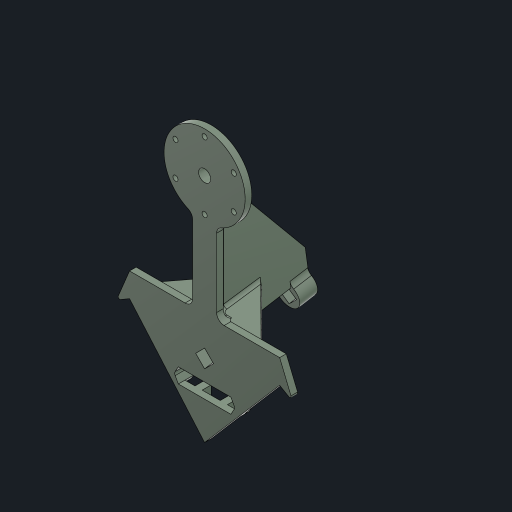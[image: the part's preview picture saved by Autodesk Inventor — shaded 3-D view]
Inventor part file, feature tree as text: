
AUTODESK INVENTOR PART (.ipt)
format: ipt  version: 2023 (Build 270158000, 158)  size: 518,144 bytes
history: native  units: mm
features: extrude x17, sketch x16, other x6, fillet x3, projected_geometry x2, mirror x1, hole x1, pattern_circular x1
ambient origin geometry x8: Origin, YZ Plane, XZ Plane, XY Plane, X Axis, Y Axis, Z Axis, Center Point
bodies: Body1 (feature_tree)
feature tree (47):
  other  "ソリッド1"
  sketch  "スケッチ1"
  extrude  "押し出し1"  Depth=2.2mm
  extrude  "押し出し2"  Depth=40.0mm
  extrude  "押し出し4"  Depth=14.3117mm
  extrude  "押し出し5"  Depth=8.0mm
  extrude  "爪"  Depth=180.0mm
  extrude  "押し出し17"  Depth=15.0mm
  extrude  "押し出し20"  Depth=14.0499mm
  extrude  "押し出し21"  Depth=30.0mm
  mirror  "ミラー1"
  extrude  "押し出し6"  Depth=25.0mm TaperAngle=0.0deg
  other  "作業平面2"
  extrude  "押し出し10"  Depth=4.0mm TaperAngle=0.0deg
  extrude  "ロッド穴"  Depth=1.6mm TaperAngle=0.0deg
  other  "作業平面3"
  extrude  "押し出し11"  TaperAngle=0.0deg  [1 undecoded]
  hole  "穴1"  [1 undecoded]
  pattern_circular  "円形状パターン1"  [2 undecoded]
  extrude  "穴延長"  Depth=1.4mm TaperAngle=0.0deg
  extrude  "押し出し12"  Depth=1.0mm
  extrude  "押し出し13"  Depth=4.2mm
  fillet  "フィレット2"  [1 undecoded]
  other  "YZ平面"
  other  "XZ平面"
  extrude  "押し出し22"  Depth=8.0mm
  fillet  "フィレット3"  Radius=5.0mm
  fillet  "フィレット4"  Radius=6.0mm
  extrude  "押し出し23"  Depth=22.4mm
  sketch  "スケッチ2"
  sketch  "スケッチ3"
  other  "作業平面1"
  sketch  "スケッチ6"
  sketch  "スケッチ7"
  sketch  "スケッチ8"
  projected_geometry  "投影ループ1"
  sketch  "スケッチ9"
  sketch  "スケッチ10"
  sketch  "スケッチ11"
  sketch  "スケッチ15"
  sketch  "スケッチ16"
  sketch  "スケッチ19"
  sketch  "スケッチ21"
  sketch  "スケッチ22"
  projected_geometry  "投影ループ2"
  sketch  "スケッチ23"
  sketch  "スケッチ24"
note: 5 required parameter values undecoded (feature->parameter linkage not recoverable at this tier; creation-order binding heuristic only, values carry confidence <= 0.55)
